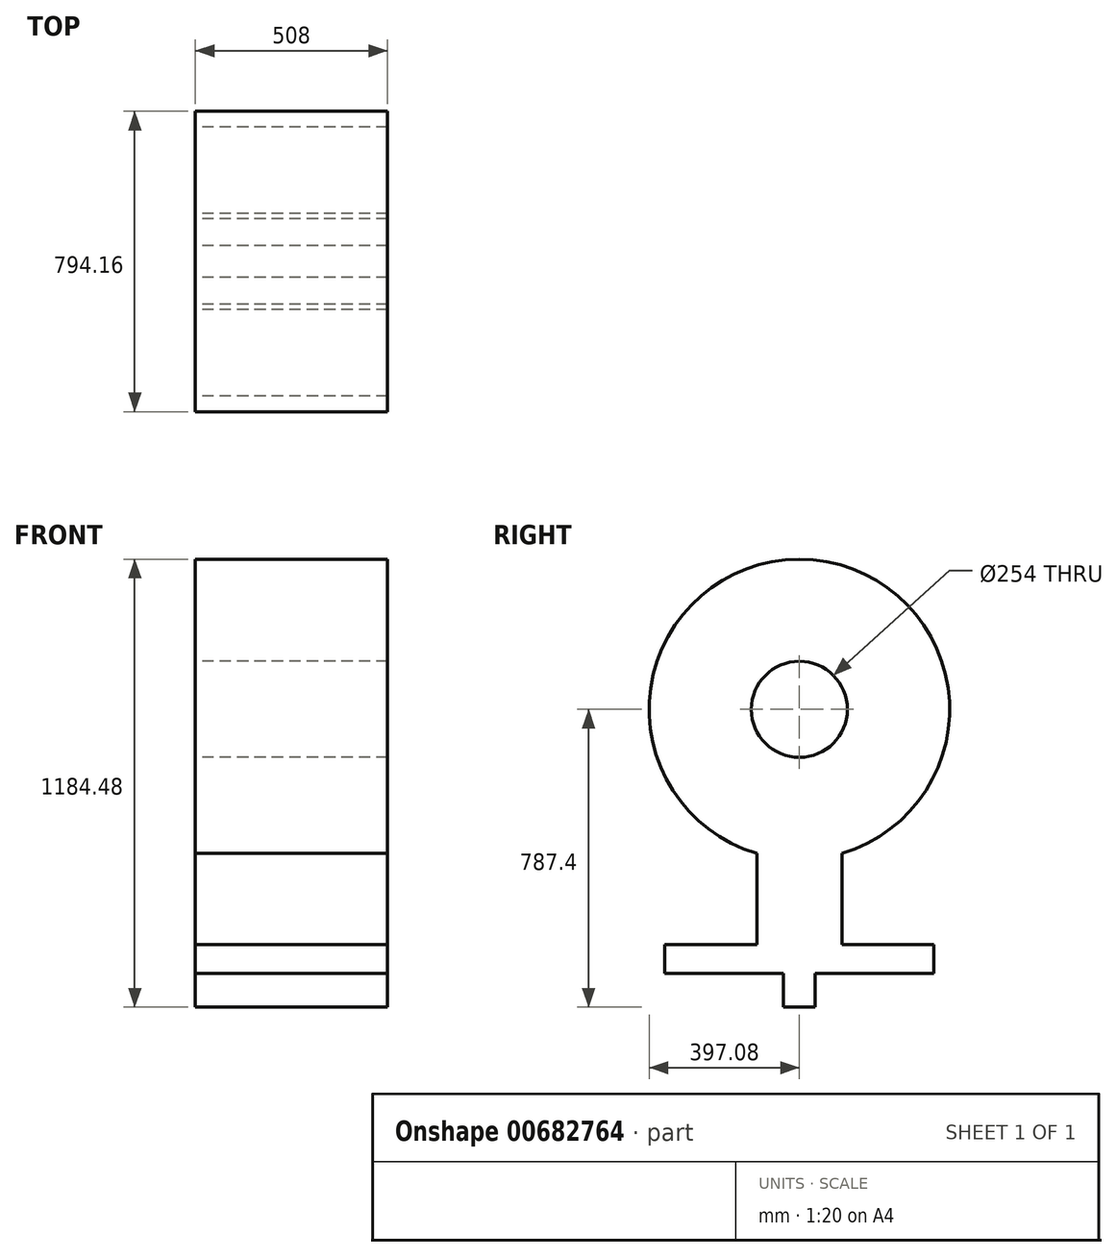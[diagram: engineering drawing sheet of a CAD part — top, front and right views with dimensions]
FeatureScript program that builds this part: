
annotation { "Feature Type Name" : "Feature", "Feature Type Description" : "" }
export const myFeature = defineFeature(function(context is Context, id is Id, definition is map)
    precondition{}
    {
        {
            var Q0;
            Q0=qCreatedBy(makeId("Right.planeOp"),FACE);
            var sketch = newSketch(context, id + "F0", { "sketchPlane" : qUnion([Q0])});
            skLineSegment(sketch, "E0.bottom", {"start": v(41.9, -63.5) * mm, "end": v(-41.91, -63.5) * mm});
            skLineSegment(sketch, "E0.top", {"start": v(41.91, 63.5) * mm, "end": v(-41.91, 63.5) * mm});
            skLineSegment(sketch, "E0.left", {"start": v(41.9, -63.5) * mm, "end": v(41.9, 63.5) * mm});
            skLineSegment(sketch, "E0.right", {"start": v(-41.91, -63.5) * mm, "end": v(-41.91, 63.5) * mm});
            skPoint(sketch, "E0.middle", {"position": v(0, 0) * mm});
            skLineSegment(sketch, "E1.bottom", {"start": v(355.6, 25.4) * mm, "end": v(-355.6, 25.4) * mm});
            skLineSegment(sketch, "E1.top", {"start": v(355.6, 101.6) * mm, "end": v(-355.6, 101.6) * mm});
            skLineSegment(sketch, "E1.left", {"start": v(355.6, 25.4) * mm, "end": v(355.6, 101.6) * mm});
            skLineSegment(sketch, "E1.right", {"start": v(-355.6, 25.4) * mm, "end": v(-355.6, 101.6) * mm});
            skPoint(sketch, "E1.middle", {"position": v(0, 63.5) * mm});
            skLineSegment(sketch, "E2", {"start": v(0, 25.4) * mm, "end": v(0, 723.9) * mm});
            skCircle(sketch, "E3", {"center": v(0, 723.9) * mm, "radius": 127 * mm});
            skCircle(sketch, "E4", {"center": v(0, 723.9) * mm, "radius": 397.08 * mm});
            skLineSegment(sketch, "E5.bottom", {"start": v(112.67, 25.4) * mm, "end": v(-112.67, 25.4) * mm});
            skLineSegment(sketch, "E5.top", {"start": v(112.67, 628.24) * mm, "end": v(-112.67, 628.24) * mm});
            skLineSegment(sketch, "E5.left", {"start": v(112.67, 25.4) * mm, "end": v(112.67, 628.24) * mm});
            skLineSegment(sketch, "E5.right", {"start": v(-112.67, 25.4) * mm, "end": v(-112.67, 628.24) * mm});
            skPoint(sketch, "E5.middle", {"position": v(0, 326.82) * mm});
            skSolve(sketch);
        }
        {
            var Q0;
            Q0 = qSketchRegion(id + "F0", true);
            extrude(context, id + "F1", {"entities" : qUnion([Q0]), "depth" : 508 * mm, "offsetDistance" : 25.4 * mm});
        }
    });
